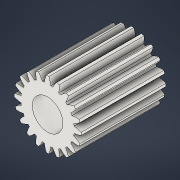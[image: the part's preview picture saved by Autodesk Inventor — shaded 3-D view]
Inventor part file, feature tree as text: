
AUTODESK INVENTOR PART (.ipt)
format: ipt  version: 2021 (Build 250183000, 183)  size: 292,352 bytes
history: native  units: mm (DEFAULTED — no unit token found)
features: plane x3, other x3, sketch x3, extrude x2
ambient origin geometry x8: Origin, YZ Plane, XZ Plane, XY Plane, X Axis, Y Axis, Z Axis, Center Point
bodies: Solid1 (feature_tree)
feature tree (11):
  extrude  "Extrusion1"  Depth=2.5mm TaperAngle=0.0deg
  plane  "Work Plane2"
  plane  "Work Plane8"
  plane  "Work Plane9"
  other  "Engrenagem reta"
  extrude  "Extrusão2"  Depth=10.0mm TaperAngle=0.0deg
  sketch  "Sketch1"  dims[d0=1.979988mm d1=2.5mm d2=0.0mm]
  sketch  "Sketch2"  dims[d3=1.8mm d4=10.0mm d5=0.0mm]
  other  "Srf1"
  sketch  "Esboço3"  dims[d16=3.597588mm d17=0.0mm d34=1.570796mm d39=0.0mm d41=0.0mm d43=3.597588mm d46=3.597588mm d47=0.0mm d48=0.0mm d49=0.9mm d50=2.5mm d51=0.0mm]
  other  "Diâmetro do flanco"
